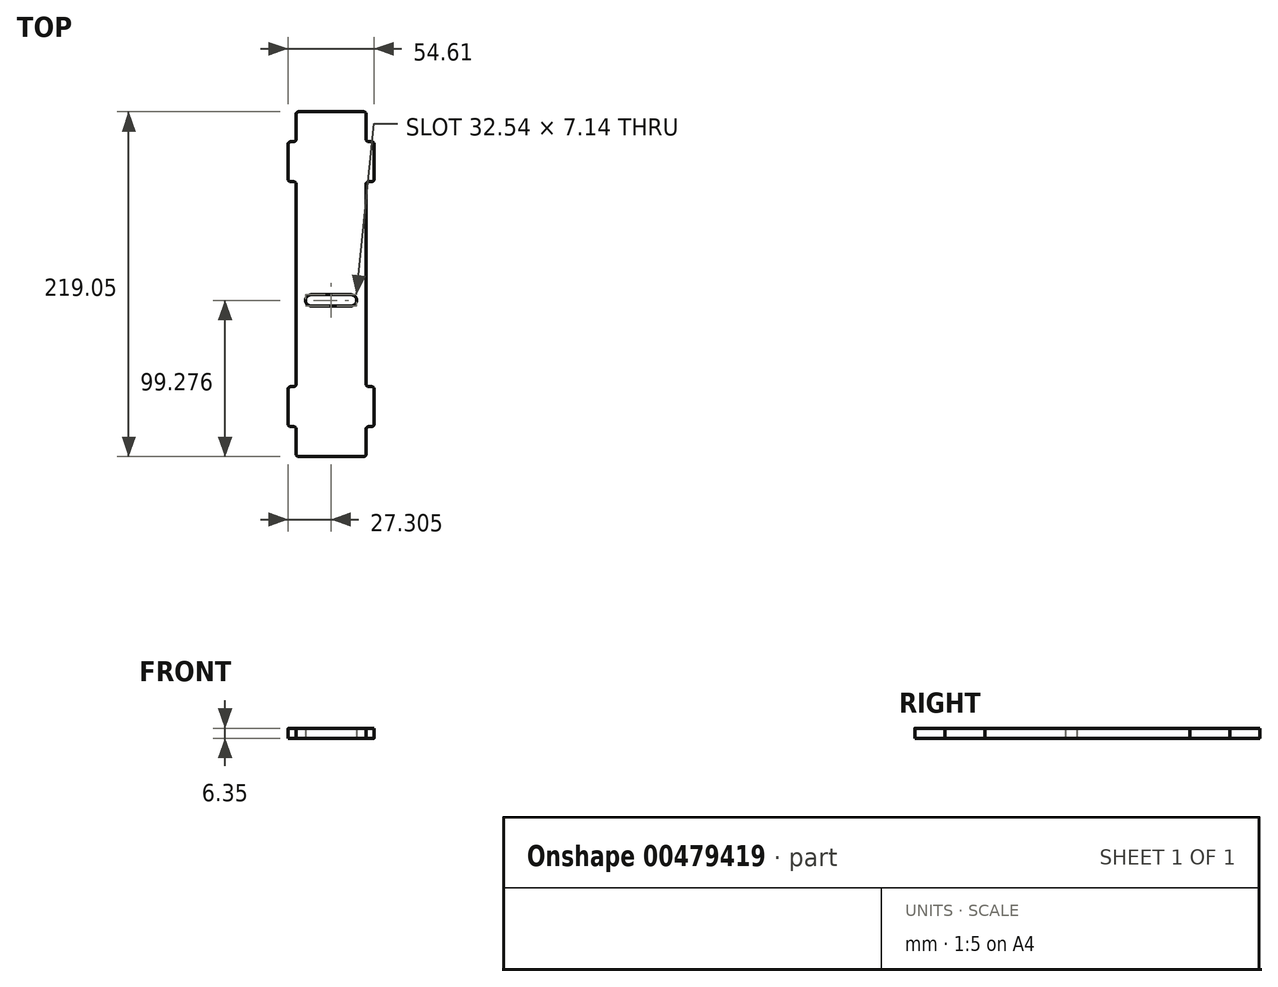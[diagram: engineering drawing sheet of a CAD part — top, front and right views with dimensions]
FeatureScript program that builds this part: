
annotation { "Feature Type Name" : "Feature", "Feature Type Description" : "" }
export const myFeature = defineFeature(function(context is Context, id is Id, definition is map)
    precondition{}
    {
        {
            var Q0;
            Q0=qCreatedBy(makeId("Top.planeOp"),FACE);
            var sketch = newSketch(context, id + "F0", { "sketchPlane" : qUnion([Q0])});
            skLineSegment(sketch, "E0", {"start": v(1.6, 0) * mm, "end": v(42.85, 0) * mm});
            skLineSegment(sketch, "E1", {"start": v(44.45, 1.6) * mm, "end": v(44.45, 17.45) * mm});
            skLineSegment(sketch, "E2", {"start": v(46.05, 19.05) * mm, "end": v(47.93, 19.05) * mm});
            skLineSegment(sketch, "E3", {"start": v(49.53, 20.65) * mm, "end": v(49.53, 42.85) * mm});
            skLineSegment(sketch, "E4", {"start": v(47.93, 44.45) * mm, "end": v(46.05, 44.45) * mm});
            skLineSegment(sketch, "E5", {"start": v(44.45, 46.05) * mm, "end": v(44.45, 173) * mm});
            skLineSegment(sketch, "E6", {"start": v(0, 173) * mm, "end": v(0, 46.05) * mm});
            skLineSegment(sketch, "E7", {"start": v(-1.6, 44.45) * mm, "end": v(-3.48, 44.45) * mm});
            skLineSegment(sketch, "E8", {"start": v(-5.08, 42.85) * mm, "end": v(-5.08, 20.65) * mm});
            skLineSegment(sketch, "E9", {"start": v(-3.48, 19.05) * mm, "end": v(-1.6, 19.05) * mm});
            skLineSegment(sketch, "E10", {"start": v(0, 17.45) * mm, "end": v(0, 1.6) * mm});
            skLineSegment(sketch, "E11", {"start": v(46.05, 174.6) * mm, "end": v(47.93, 174.6) * mm});
            skLineSegment(sketch, "E12", {"start": v(49.53, 176.2) * mm, "end": v(49.53, 198.4) * mm});
            skLineSegment(sketch, "E13", {"start": v(47.93, 200) * mm, "end": v(46.05, 200) * mm});
            skLineSegment(sketch, "E14", {"start": v(44.45, 201.6) * mm, "end": v(44.45, 217.45) * mm});
            skLineSegment(sketch, "E15", {"start": v(42.85, 219.05) * mm, "end": v(1.6, 219.05) * mm});
            skLineSegment(sketch, "E16", {"start": v(0, 217.45) * mm, "end": v(0, 201.6) * mm});
            skLineSegment(sketch, "E17", {"start": v(-1.6, 200) * mm, "end": v(-3.48, 200) * mm});
            skLineSegment(sketch, "E18", {"start": v(-5.08, 198.4) * mm, "end": v(-5.08, 176.2) * mm});
            skLineSegment(sketch, "E19", {"start": v(-3.48, 174.6) * mm, "end": v(-1.6, 174.6) * mm});
            skPoint(sketch, "E20.visualSharp", {"position": v(0, 219.05) * mm});
            skArc(sketch, "E20.filletArc", {"start": v(1.6, 219.05) * mm, "mid": v(0.47, 218.58) * mm, "end": v(0, 217.45) * mm});
            skPoint(sketch, "E21.visualSharp", {"position": v(44.45, 219.05) * mm});
            skArc(sketch, "E21.filletArc", {"start": v(44.45, 217.45) * mm, "mid": v(43.98, 218.58) * mm, "end": v(42.85, 219.05) * mm});
            skPoint(sketch, "E22.visualSharp", {"position": v(44.45, 200) * mm});
            skArc(sketch, "E22.filletArc", {"start": v(44.45, 201.6) * mm, "mid": v(44.92, 200.47) * mm, "end": v(46.05, 200) * mm});
            skPoint(sketch, "E23.visualSharp", {"position": v(49.53, 200) * mm});
            skArc(sketch, "E23.filletArc", {"start": v(49.53, 198.4) * mm, "mid": v(49.06, 199.53) * mm, "end": v(47.93, 200) * mm});
            skPoint(sketch, "E24.visualSharp", {"position": v(49.53, 174.6) * mm});
            skArc(sketch, "E24.filletArc", {"start": v(47.93, 174.6) * mm, "mid": v(49.06, 175.07) * mm, "end": v(49.53, 176.2) * mm});
            skPoint(sketch, "E25.visualSharp", {"position": v(44.45, 174.6) * mm});
            skArc(sketch, "E25.filletArc", {"start": v(46.05, 174.6) * mm, "mid": v(44.92, 174.13) * mm, "end": v(44.45, 173) * mm});
            skPoint(sketch, "E26.visualSharp", {"position": v(0, 174.6) * mm});
            skArc(sketch, "E26.filletArc", {"start": v(0, 173) * mm, "mid": v(-0.47, 174.13) * mm, "end": v(-1.6, 174.6) * mm});
            skPoint(sketch, "E27.visualSharp", {"position": v(-5.08, 174.6) * mm});
            skArc(sketch, "E27.filletArc", {"start": v(-5.08, 176.2) * mm, "mid": v(-4.61, 175.07) * mm, "end": v(-3.48, 174.6) * mm});
            skPoint(sketch, "E28.visualSharp", {"position": v(-5.08, 200) * mm});
            skArc(sketch, "E28.filletArc", {"start": v(-3.48, 200) * mm, "mid": v(-4.61, 199.53) * mm, "end": v(-5.08, 198.4) * mm});
            skPoint(sketch, "E29.visualSharp", {"position": v(0, 200) * mm});
            skArc(sketch, "E29.filletArc", {"start": v(-1.6, 200) * mm, "mid": v(-0.47, 200.47) * mm, "end": v(0, 201.6) * mm});
            skPoint(sketch, "E30.visualSharp", {"position": v(0, 44.45) * mm});
            skArc(sketch, "E30.filletArc", {"start": v(-1.6, 44.45) * mm, "mid": v(-0.47, 44.92) * mm, "end": v(0, 46.05) * mm});
            skPoint(sketch, "E31.visualSharp", {"position": v(-5.08, 44.45) * mm});
            skArc(sketch, "E31.filletArc", {"start": v(-3.48, 44.45) * mm, "mid": v(-4.61, 43.98) * mm, "end": v(-5.08, 42.85) * mm});
            skPoint(sketch, "E32.visualSharp", {"position": v(-5.08, 19.05) * mm});
            skArc(sketch, "E32.filletArc", {"start": v(-5.08, 20.65) * mm, "mid": v(-4.61, 19.52) * mm, "end": v(-3.48, 19.05) * mm});
            skPoint(sketch, "E33.visualSharp", {"position": v(0, 19.05) * mm});
            skArc(sketch, "E33.filletArc", {"start": v(0, 17.45) * mm, "mid": v(-0.47, 18.58) * mm, "end": v(-1.6, 19.05) * mm});
            skPoint(sketch, "E34.visualSharp", {"position": v(0, 0) * mm});
            skArc(sketch, "E34.filletArc", {"start": v(0, 1.6) * mm, "mid": v(0.47, 0.47) * mm, "end": v(1.6, 0) * mm});
            skPoint(sketch, "E35.visualSharp", {"position": v(44.45, 0) * mm});
            skArc(sketch, "E35.filletArc", {"start": v(42.85, 0) * mm, "mid": v(43.98, 0.47) * mm, "end": v(44.45, 1.6) * mm});
            skPoint(sketch, "E36.visualSharp", {"position": v(44.45, 19.05) * mm});
            skArc(sketch, "E36.filletArc", {"start": v(46.05, 19.05) * mm, "mid": v(44.92, 18.58) * mm, "end": v(44.45, 17.45) * mm});
            skPoint(sketch, "E37.visualSharp", {"position": v(49.53, 19.05) * mm});
            skArc(sketch, "E37.filletArc", {"start": v(47.93, 19.05) * mm, "mid": v(49.06, 19.52) * mm, "end": v(49.53, 20.65) * mm});
            skPoint(sketch, "E38.visualSharp", {"position": v(49.53, 44.45) * mm});
            skArc(sketch, "E38.filletArc", {"start": v(49.53, 42.85) * mm, "mid": v(49.06, 43.98) * mm, "end": v(47.93, 44.45) * mm});
            skPoint(sketch, "E39.visualSharp", {"position": v(44.45, 44.45) * mm});
            skArc(sketch, "E39.filletArc", {"start": v(44.45, 46.05) * mm, "mid": v(44.92, 44.92) * mm, "end": v(46.05, 44.45) * mm});
            skCircle(sketch, "E40", {"center": v(9.52, 99.28) * mm, "radius": 3.57 * mm});
            skCircle(sketch, "E41", {"center": v(34.92, 99.28) * mm, "radius": 3.57 * mm});
            skLineSegment(sketch, "E42", {"start": v(9.52, 102.84) * mm, "end": v(34.92, 102.84) * mm});
            skLineSegment(sketch, "E43", {"start": v(9.52, 95.7) * mm, "end": v(34.92, 95.7) * mm});
            skSolve(sketch);
        }
        {
            var Q0;
            Q0 = qSketchRegion(id + "F0", true);
            extrude(context, id + "F1", {"entities" : qUnion([Q0]), "depth" : 6.35 * mm, "offsetDistance" : 25.4 * mm});
        }
    });
